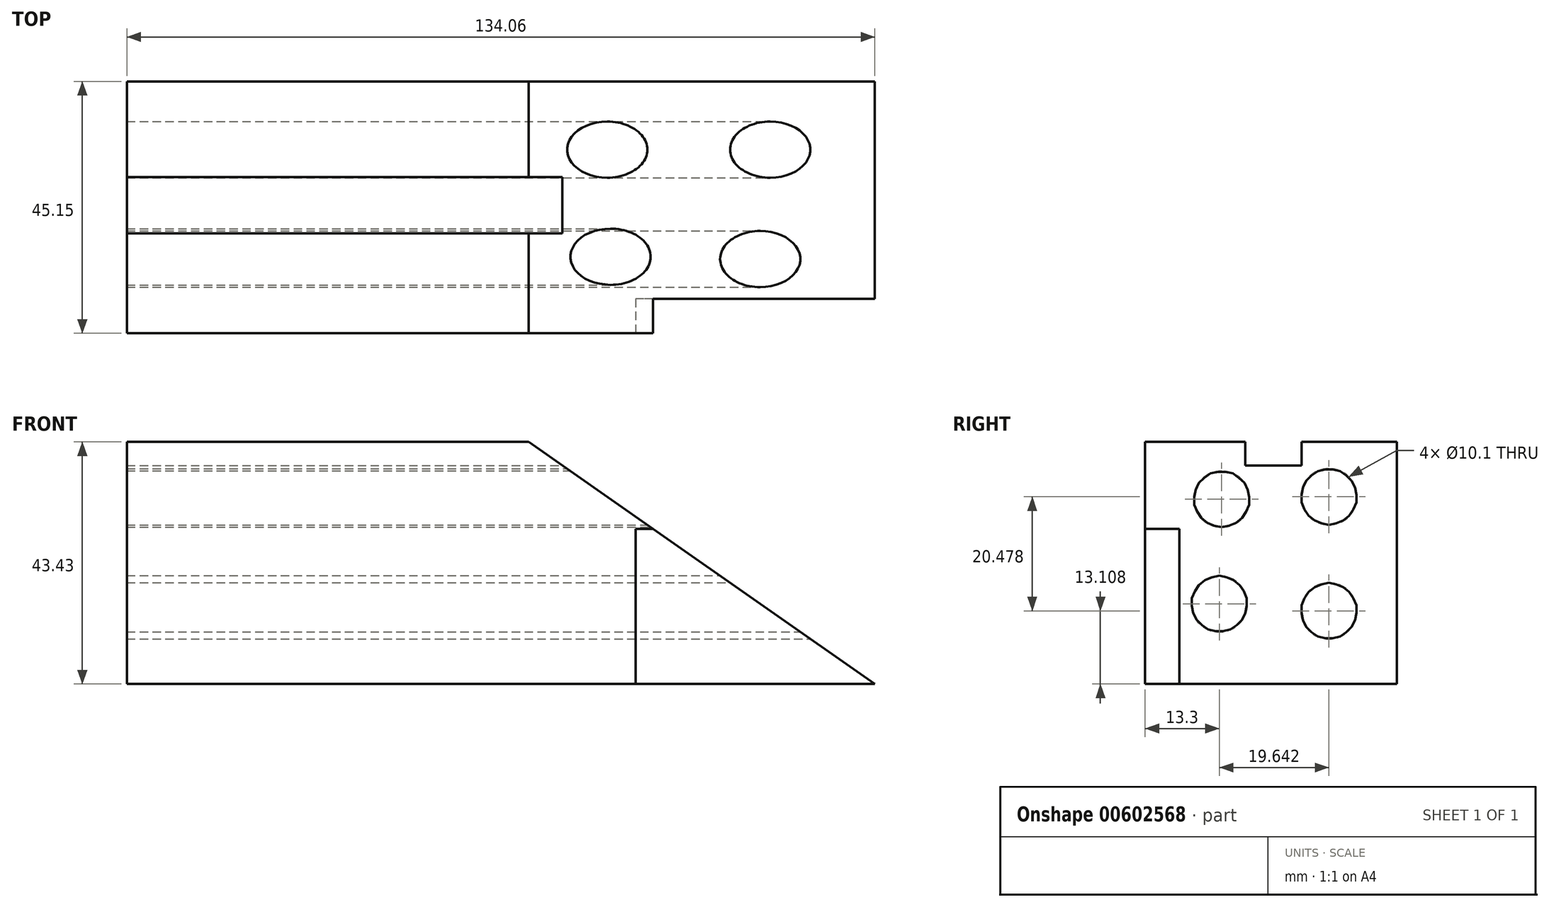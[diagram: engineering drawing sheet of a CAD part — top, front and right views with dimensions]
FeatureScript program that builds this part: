
annotation { "Feature Type Name" : "Feature", "Feature Type Description" : "" }
export const myFeature = defineFeature(function(context is Context, id is Id, definition is map)
    precondition{}
    {
        {
            var Q0;
            Q0=qCreatedBy(makeId("Top.planeOp"),FACE);
            var sketch = newSketch(context, id + "F0", { "sketchPlane" : qUnion([Q0])});
            skLineSegment(sketch, "E0.bottom", {"start": v(-66.8, -21.75) * mm, "end": v(67.27, -21.75) * mm});
            skLineSegment(sketch, "E0.top", {"start": v(-66.8, 23.4) * mm, "end": v(67.27, 23.4) * mm});
            skLineSegment(sketch, "E0.left", {"start": v(-66.8, -21.75) * mm, "end": v(-66.8, 23.4) * mm});
            skLineSegment(sketch, "E0.right", {"start": v(67.27, -21.75) * mm, "end": v(67.27, 23.4) * mm});
            skSolve(sketch);
        }
        {
            var Q0;
            Q0=sQuery(id+"F0.wireOp",EDGE,"E0.right");
            cPlane(context, id + "F1", {"entities" : qUnion([Q0]), "cplaneType" : CPlaneType.LINE_ANGLE, "offset" : 25.4 * mm, "angle" : 35 * degree, "width" : 152.4 * mm, "height" : 152.4 * mm});
        }
        {
            var Q0;
            Q0 = qSketchRegion(id + "F0", true);
            var Q1;
            Q1=qCreatedBy(id+"F1.planeOp",FACE);
            extrude(context, id + "F2", {"entities" : qUnion([Q0]), "endBound" : BoundingType.UP_TO_SURFACE, "depth" : 40.13 * mm, "endBoundEntityFace" : qUnion([Q1]), "offsetDistance" : 25.4 * mm});
        }
        {
            var Q0;
            Q0=makeQuery(id+"F2.opExtrude","CAP_FACE",FACE,{"disambiguationData":[OSD([sQuery(id+"F0.wireOp",EDGE,"E0.bottom"),sQuery(id+"F0.wireOp",EDGE,"E0.top"),sQuery(id+"F0.wireOp",EDGE,"E0.left"),sQuery(id+"F0.wireOp",EDGE,"E0.right")])],"isStart":true});
            cPlane(context, id + "F3", {"entities" : qUnion([Q0]), "cplaneType" : CPlaneType.OFFSET, "offset" : 43.43 * mm, "oppositeDirection" : true, "width" : 152.4 * mm, "height" : 152.4 * mm});
        }
        {
            var Q0;
            Q0=qCreatedBy(id+"F3.planeOp",FACE);
            var sketch = newSketch(context, id + "F4", { "sketchPlane" : qUnion([Q0])});
            skLineSegment(sketch, "E1.bottom", {"start": v(-97.91, -48.38) * mm, "end": v(144.9, -48.38) * mm});
            skLineSegment(sketch, "E1.top", {"start": v(-97.91, 79.8) * mm, "end": v(144.9, 79.8) * mm});
            skLineSegment(sketch, "E1.left", {"start": v(-97.91, -48.38) * mm, "end": v(-97.91, 79.8) * mm});
            skLineSegment(sketch, "E1.right", {"start": v(144.9, -48.38) * mm, "end": v(144.9, 79.8) * mm});
            skSolve(sketch);
        }
        {
            var Q0;
            Q0 = qSketchRegion(id + "F4", true);
            extrude(context, id + "F5", {"entities" : qUnion([Q0]), "operationType" : NewBodyOperationType.REMOVE, "oppositeDirection" : true, "depth" : 69.1 * mm, "offsetDistance" : 25.4 * mm});
        }
        {
            var Q0;
            Q0=makeQuery(id+"F2.opExtrude","SWEPT_FACE",FACE,{"disambiguationData":[OSD([sQuery(id+"F0.wireOp",EDGE,"E0.left")])]});
            cPlane(context, id + "F6", {"entities" : qUnion([Q0]), "cplaneType" : CPlaneType.OFFSET, "offset" : 91.19 * mm, "oppositeDirection" : true, "width" : 152.4 * mm, "height" : 152.4 * mm});
        }
        {
            var Q0;
            Q0=qCreatedBy(id+"F6.planeOp",FACE);
            var sketch = newSketch(context, id + "F7", { "sketchPlane" : qUnion([Q0])});
            skLineSegment(sketch, "E2.bottom", {"start": v(24.06, 27.85) * mm, "end": v(15.6, 27.85) * mm});
            skLineSegment(sketch, "E2.top", {"start": v(24.06, -3.1) * mm, "end": v(15.6, -3.1) * mm});
            skLineSegment(sketch, "E2.left", {"start": v(24.06, 27.85) * mm, "end": v(24.06, -3.1) * mm});
            skLineSegment(sketch, "E2.right", {"start": v(15.6, 27.85) * mm, "end": v(15.6, -3.1) * mm});
            skSolve(sketch);
        }
        {
            var Q0;
            Q0 = qSketchRegion(id + "F7", true);
            extrude(context, id + "F8", {"entities" : qUnion([Q0]), "operationType" : NewBodyOperationType.REMOVE, "oppositeDirection" : true, "depth" : 81.53 * mm, "offsetDistance" : 25.4 * mm});
        }
        {
            var Q0;
            Q0=qCreatedBy(id+"F6.planeOp",FACE);
            var sketch = newSketch(context, id + "F9", { "sketchPlane" : qUnion([Q0])});
            skCircle(sketch, "E3", {"center": v(8.03, 33.17) * mm, "radius": 5.05 * mm});
            skCircle(sketch, "E4", {"center": v(-11.2, 33.59) * mm, "radius": 5.05 * mm});
            skCircle(sketch, "E5", {"center": v(-11.2, 13.1) * mm, "radius": 5.05 * mm});
            skCircle(sketch, "E6", {"center": v(8.45, 14.36) * mm, "radius": 5.05 * mm});
            skSolve(sketch);
        }
        {
            var Q0;
            Q0 = qSketchRegion(id + "F9", true);
            extrude(context, id + "F10", {"entities" : qUnion([Q0]), "operationType" : NewBodyOperationType.REMOVE, "depth" : 222.76 * mm, "offsetDistance" : 25.4 * mm});
        }
        {
            var Q0;
            Q0 = qSketchRegion(id + "F9", true);
            extrude(context, id + "F11", {"entities" : qUnion([Q0]), "operationType" : NewBodyOperationType.REMOVE, "oppositeDirection" : true, "depth" : 75.7 * mm, "offsetDistance" : 25.4 * mm});
        }
        {
            var Q0;
            Q0=qCreatedBy(id+"F6.planeOp",FACE);
            var sketch = newSketch(context, id + "F12", { "sketchPlane" : qUnion([Q0])});
            skLineSegment(sketch, "E7.bottom", {"start": v(3.82, 44.4) * mm, "end": v(-6.3, 44.4) * mm});
            skLineSegment(sketch, "E7.top", {"start": v(3.82, 39.19) * mm, "end": v(-6.3, 39.19) * mm});
            skLineSegment(sketch, "E7.left", {"start": v(3.82, 44.4) * mm, "end": v(3.82, 39.19) * mm});
            skLineSegment(sketch, "E7.right", {"start": v(-6.3, 44.4) * mm, "end": v(-6.3, 39.19) * mm});
            skSolve(sketch);
        }
        {
            var Q0;
            Q0 = qSketchRegion(id + "F12", true);
            extrude(context, id + "F13", {"entities" : qUnion([Q0]), "operationType" : NewBodyOperationType.REMOVE, "depth" : 157.73 * mm, "offsetDistance" : 25.4 * mm});
        }
    });
